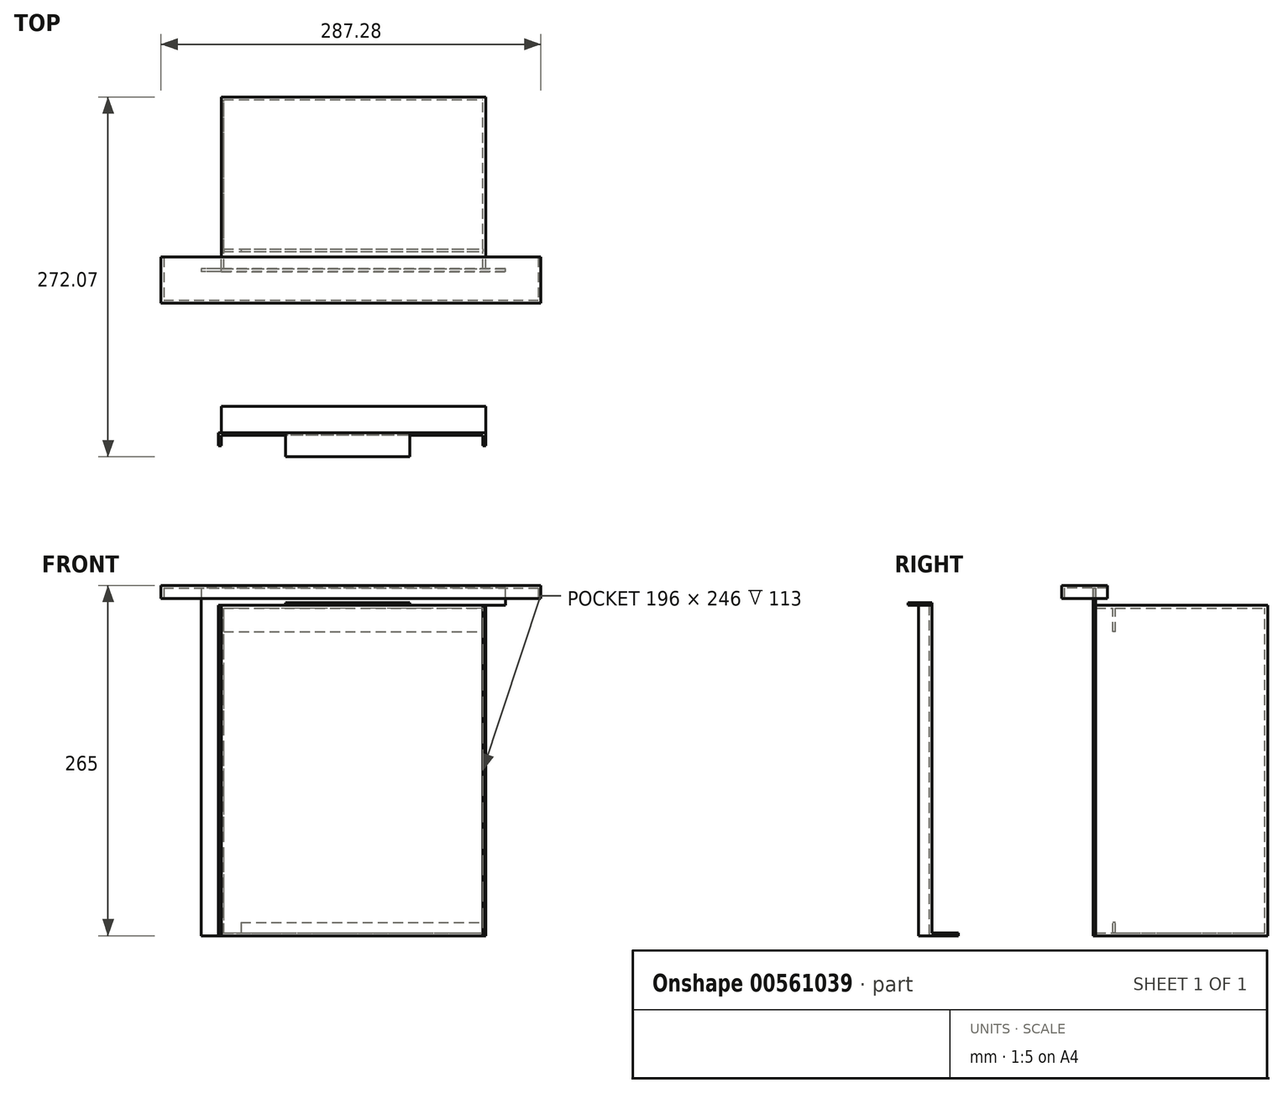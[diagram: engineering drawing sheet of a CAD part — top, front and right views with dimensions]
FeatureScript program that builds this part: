
annotation { "Feature Type Name" : "Feature", "Feature Type Description" : "" }
export const myFeature = defineFeature(function(context is Context, id is Id, definition is map)
    precondition{}
    {
        {
            var Q0;
            Q0=qCreatedBy(makeId("Front.planeOp"),FACE);
            var sketch = newSketch(context, id + "F0", { "sketchPlane" : qUnion([Q0])});
            skLineSegment(sketch, "E0.bottom", {"start": v(80.63, 0) * mm, "end": v(280.63, 0) * mm});
            skLineSegment(sketch, "E0.top", {"start": v(80.63, 250) * mm, "end": v(280.63, 250) * mm});
            skLineSegment(sketch, "E0.left", {"start": v(80.63, 0) * mm, "end": v(80.63, 250) * mm});
            skLineSegment(sketch, "E0.right", {"start": v(280.63, 0) * mm, "end": v(280.63, 250) * mm});
            skSolve(sketch);
        }
        {
            var Q0;
            Q0=makeQuery(id+"F0.imprint","IMPRINT",FACE,{"disambiguationData":[TD([[makeQuery(id+"F0.imprint","IMPRINT",EDGE,{"derivedFrom":sQuery(id+"F0.wireOp",EDGE,"E0.bottom")}),1.0]])]});
            extrude(context, id + "F1", {"entities" : qUnion([Q0]), "depth" : 130 * mm, "offsetDistance" : 25 * mm});
        }
        {
            var Q0;
            Q0=makeQuery(id+"F1.opExtrude","CAP_FACE",FACE,{"disambiguationData":[OSD([sQuery(id+"F0.wireOp",EDGE,"E0.bottom"),sQuery(id+"F0.wireOp",EDGE,"E0.top"),sQuery(id+"F0.wireOp",EDGE,"E0.left"),sQuery(id+"F0.wireOp",EDGE,"E0.right")])],"isStart":false});
            shell(context, id + "F2", {"entities" : qUnion([Q0]), "thickness" : 2 * mm});
        }
        {
            var Q0;
            Q0=makeQuery(id+"F2.opShell","OFFSET_FACE",FACE,{"disambiguationData":[OSD([sQuery(id+"F0.wireOp",EDGE,"E0.bottom"),sQuery(id+"F0.wireOp",EDGE,"E0.top"),sQuery(id+"F0.wireOp",EDGE,"E0.left"),sQuery(id+"F0.wireOp",EDGE,"E0.right")])]});
            cPlane(context, id + "F3", {"entities" : qUnion([Q0]), "cplaneType" : CPlaneType.OFFSET, "offset" : 115 * mm, "width" : 150 * mm, "height" : 150 * mm});
        }
        {
            var Q0;
            Q0=qCreatedBy(id+"F3.planeOp",FACE);
            var sketch = newSketch(context, id + "F4", { "sketchPlane" : qUnion([Q0])});
            skLineSegment(sketch, "E1.bottom", {"start": v(80.63, 250) * mm, "end": v(280.63, 250) * mm});
            skLineSegment(sketch, "E1.top", {"start": v(80.63, 230) * mm, "end": v(280.63, 230) * mm});
            skLineSegment(sketch, "E1.left", {"start": v(80.63, 250) * mm, "end": v(80.63, 230) * mm});
            skLineSegment(sketch, "E1.right", {"start": v(280.63, 250) * mm, "end": v(280.63, 230) * mm});
            skLineSegment(sketch, "E2.bottom", {"start": v(80.63, 230) * mm, "end": v(95.63, 230) * mm});
            skLineSegment(sketch, "E2.top", {"start": v(80.63, 0) * mm, "end": v(95.63, 0) * mm});
            skLineSegment(sketch, "E2.left", {"start": v(80.63, 230) * mm, "end": v(80.63, 0) * mm});
            skLineSegment(sketch, "E2.right", {"start": v(95.63, 230) * mm, "end": v(95.63, 0) * mm});
            skLineSegment(sketch, "E3.bottom", {"start": v(95.63, 0) * mm, "end": v(280.63, 0) * mm});
            skLineSegment(sketch, "E3.top", {"start": v(95.63, 10) * mm, "end": v(280.63, 10) * mm});
            skLineSegment(sketch, "E3.left", {"start": v(95.63, 0) * mm, "end": v(95.63, 10) * mm});
            skLineSegment(sketch, "E3.right", {"start": v(280.63, 0) * mm, "end": v(280.63, 10) * mm});
            skLineSegment(sketch, "E4.bottom", {"start": v(280.63, 10) * mm, "end": v(265.63, 10) * mm});
            skLineSegment(sketch, "E4.top", {"start": v(280.63, 230) * mm, "end": v(265.63, 230) * mm});
            skLineSegment(sketch, "E4.left", {"start": v(280.63, 10) * mm, "end": v(280.63, 230) * mm});
            skLineSegment(sketch, "E4.right", {"start": v(265.63, 10) * mm, "end": v(265.63, 230) * mm});
            skSolve(sketch);
        }
        {
            var Q0;
            Q0=makeQuery(id+"F4.imprint","IMPRINT",FACE,{"disambiguationData":[TD([[makeQuery(id+"F4.imprint","IMPRINT",EDGE,{"derivedFrom":sQuery(id+"F4.wireOp",EDGE,"E1.bottom")}),-1.0]])]});
            var Q1;
            Q1=makeQuery(id+"F4.imprint","IMPRINT",FACE,{"disambiguationData":[TD([[makeQuery(id+"F4.imprint","IMPRINT",EDGE,{"derivedFrom":sQuery(id+"F4.wireOp",EDGE,"E2.bottom")}),-1.0]])]});
            var Q2;
            Q2=makeQuery(id+"F4.imprint","IMPRINT",FACE,{"disambiguationData":[TD([[makeQuery(id+"F4.imprint","IMPRINT",EDGE,{"derivedFrom":sQuery(id+"F4.wireOp",EDGE,"E4.bottom")}),-1.0]])]});
            var Q3;
            Q3=makeQuery(id+"F4.imprint","IMPRINT",FACE,{"disambiguationData":[TD([[makeQuery(id+"F4.imprint","IMPRINT",EDGE,{"derivedFrom":sQuery(id+"F4.wireOp",EDGE,"E3.bottom")}),1.0]])]});
            extrude(context, id + "F5", {"entities" : qUnion([Q0, Q1, Q2, Q3]), "operationType" : NewBodyOperationType.ADD, "oppositeDirection" : true, "depth" : 2 * mm, "offsetDistance" : 25 * mm});
        }
        {
            var Q0;
            Q0=makeQuery(id+"F0.imprint","IMPRINT",FACE,{"disambiguationData":[TD([[makeQuery(id+"F0.imprint","IMPRINT",EDGE,{"derivedFrom":sQuery(id+"F0.wireOp",EDGE,"E0.bottom")}),1.0]])]});
            cPlane(context, id + "F6", {"entities" : qUnion([Q0]), "cplaneType" : CPlaneType.OFFSET, "offset" : 130 * mm, "width" : 150 * mm, "height" : 150 * mm});
        }
        {
            var Q0;
            Q0=qCreatedBy(id+"F6.planeOp",FACE);
            var sketch = newSketch(context, id + "F7", { "sketchPlane" : qUnion([Q0])});
            skLineSegment(sketch, "E5.bottom", {"start": v(80.63, 250) * mm, "end": v(65.63, 250) * mm});
            skLineSegment(sketch, "E5.top", {"start": v(80.63, 0) * mm, "end": v(65.63, 0) * mm});
            skLineSegment(sketch, "E5.left", {"start": v(80.63, 250) * mm, "end": v(80.63, 0) * mm});
            skLineSegment(sketch, "E5.right", {"start": v(65.63, 250) * mm, "end": v(65.63, 0) * mm});
            skLineSegment(sketch, "E6.bottom", {"start": v(65.63, 250) * mm, "end": v(295.63, 250) * mm});
            skLineSegment(sketch, "E6.top", {"start": v(65.63, 265) * mm, "end": v(295.63, 265) * mm});
            skLineSegment(sketch, "E6.left", {"start": v(65.63, 250) * mm, "end": v(65.63, 265) * mm});
            skLineSegment(sketch, "E6.right", {"start": v(295.63, 250) * mm, "end": v(295.63, 265) * mm});
            skLineSegment(sketch, "E7.bottom", {"start": v(295.63, 250) * mm, "end": v(280.63, 250) * mm});
            skLineSegment(sketch, "E7.top", {"start": v(295.63, 0) * mm, "end": v(280.63, 0) * mm});
            skLineSegment(sketch, "E7.left", {"start": v(295.63, 250) * mm, "end": v(295.63, 0) * mm});
            skLineSegment(sketch, "E7.right", {"start": v(280.63, 250) * mm, "end": v(280.63, 0) * mm});
            skLineSegment(sketch, "E8.top", {"start": v(280.63, 0) * mm, "end": v(65.63, 0) * mm});
            skLineSegment(sketch, "E8.left", {"start": v(280.63, 0) * mm, "end": v(280.63, 0) * mm});
            skSolve(sketch);
        }
        {
            var Q0;
            {var subQ0=sQuery(id+"F7.wireOp",EDGE,"E5.left");Q0=makeQuery(id+"F7.imprint","IMPRINT",FACE,{"disambiguationData":[TD([[makeQuery(id+"F7.imprint","IMPRINT",EDGE,{"derivedFrom":subQ0}),-1.0]])]});}
            var Q1;
            Q1=makeQuery(id+"F7.imprint","IMPRINT",FACE,{"disambiguationData":[TD([[makeQuery(id+"F7.imprint","IMPRINT",EDGE,{"derivedFrom":sQuery(id+"F7.wireOp",EDGE,"E6.top")}),-1.0]])]});
            var Q2;
            Q2=makeQuery(id+"F7.imprint","IMPRINT",FACE,{"disambiguationData":[TD([[makeQuery(id+"F7.imprint","IMPRINT",EDGE,{"derivedFrom":sQuery(id+"F7.wireOp",EDGE,"E7.bottom")}),1.0]])]});
            extrude(context, id + "F8", {"entities" : qUnion([Q0, Q1, Q2]), "operationType" : NewBodyOperationType.ADD, "depth" : 2 * mm, "offsetDistance" : 25 * mm});
        }
        {
            var Q0;
            Q0=makeQuery(id+"F0.imprint","IMPRINT",FACE,{"disambiguationData":[TD([[makeQuery(id+"F0.imprint","IMPRINT",EDGE,{"derivedFrom":sQuery(id+"F0.wireOp",EDGE,"E0.bottom")}),1.0]])]});
            cPlane(context, id + "F9", {"entities" : qUnion([Q0]), "cplaneType" : CPlaneType.OFFSET, "offset" : 254 * mm, "width" : 150 * mm, "height" : 150 * mm});
        }
        {
            var Q0;
            Q0=qCreatedBy(id+"F9.planeOp",FACE);
            var sketch = newSketch(context, id + "F10", { "sketchPlane" : qUnion([Q0])});
            skLineSegment(sketch, "E9.bottom", {"start": v(280.63, 250) * mm, "end": v(80.63, 250) * mm});
            skLineSegment(sketch, "E9.top", {"start": v(280.63, 0) * mm, "end": v(80.63, 0) * mm});
            skLineSegment(sketch, "E9.left", {"start": v(280.63, 250) * mm, "end": v(280.63, 0) * mm});
            skLineSegment(sketch, "E9.right", {"start": v(80.63, 250) * mm, "end": v(80.63, 0) * mm});
            skSolve(sketch);
        }
        {
            var Q0;
            Q0=makeQuery(id+"F10.imprint","IMPRINT",FACE,{"disambiguationData":[TD([[makeQuery(id+"F10.imprint","IMPRINT",EDGE,{"derivedFrom":sQuery(id+"F10.wireOp",EDGE,"E9.bottom")}),1.0]])]});
            extrude(context, id + "F11", {"entities" : qUnion([Q0]), "depth" : 2 * mm, "offsetDistance" : 25 * mm});
        }
        {
            var Q0;
            Q0=sQuery(id+"F10.wireOp",EDGE,"E9.right");
            cPlane(context, id + "F12", {"entities" : qUnion([Q0]), "cplaneType" : CPlaneType.LINE_ANGLE, "offset" : 25 * mm, "angle" : 0 * degree, "width" : 150 * mm, "height" : 150 * mm});
        }
        {
            var Q0;
            Q0=sQuery(id+"F10.wireOp",EDGE,"E9.left");
            cPlane(context, id + "F13", {"entities" : qUnion([Q0]), "cplaneType" : CPlaneType.LINE_ANGLE, "offset" : 25 * mm, "angle" : 0 * degree, "width" : 150 * mm, "height" : 150 * mm});
        }
        {
            var Q0;
            Q0=sQuery(id+"F10.wireOp",EDGE,"E9.top");
            cPlane(context, id + "F14", {"entities" : qUnion([Q0]), "cplaneType" : CPlaneType.LINE_ANGLE, "offset" : 25 * mm, "angle" : 90 * degree, "width" : 150 * mm, "height" : 150 * mm});
        }
        {
            var Q0;
            Q0=qCreatedBy(id+"F12.planeOp",FACE);
            var sketch = newSketch(context, id + "F15", { "sketchPlane" : qUnion([Q0])});
            skLineSegment(sketch, "E10.bottom", {"start": v(254, 250) * mm, "end": v(264, 250) * mm});
            skLineSegment(sketch, "E10.top", {"start": v(254, 0) * mm, "end": v(264, 0) * mm});
            skLineSegment(sketch, "E10.left", {"start": v(254, 250) * mm, "end": v(254, 0) * mm});
            skLineSegment(sketch, "E10.right", {"start": v(264, 250) * mm, "end": v(264, 0) * mm});
            skSolve(sketch);
        }
        {
            var Q0;
            Q0=makeQuery(id+"F15.imprint","IMPRINT",FACE,{"disambiguationData":[TD([[makeQuery(id+"F15.imprint","IMPRINT",EDGE,{"derivedFrom":sQuery(id+"F15.wireOp",EDGE,"E10.bottom")}),-1.0]])]});
            extrude(context, id + "F16", {"entities" : qUnion([Q0]), "operationType" : NewBodyOperationType.ADD, "depth" : 2 * mm, "offsetDistance" : 25 * mm});
        }
        {
            var Q0;
            Q0=qCreatedBy(id+"F13.planeOp",FACE);
            var sketch = newSketch(context, id + "F17", { "sketchPlane" : qUnion([Q0])});
            skLineSegment(sketch, "E11.bottom", {"start": v(254, 250) * mm, "end": v(264, 250) * mm});
            skLineSegment(sketch, "E11.top", {"start": v(254, 0) * mm, "end": v(264, 0) * mm});
            skLineSegment(sketch, "E11.left", {"start": v(254, 250) * mm, "end": v(254, 0) * mm});
            skLineSegment(sketch, "E11.right", {"start": v(264, 250) * mm, "end": v(264, 0) * mm});
            skSolve(sketch);
        }
        {
            var Q0;
            Q0=makeQuery(id+"F17.imprint","IMPRINT",FACE,{"disambiguationData":[TD([[makeQuery(id+"F17.imprint","IMPRINT",EDGE,{"derivedFrom":sQuery(id+"F17.wireOp",EDGE,"E11.bottom")}),-1.0]])]});
            extrude(context, id + "F18", {"entities" : qUnion([Q0]), "operationType" : NewBodyOperationType.ADD, "depth" : 2 * mm, "offsetDistance" : 25 * mm});
        }
        {
            var Q0;
            Q0=qCreatedBy(id+"F14.planeOp",FACE);
            var sketch = newSketch(context, id + "F19", { "sketchPlane" : qUnion([Q0])});
            skLineSegment(sketch, "E12.bottom", {"start": v(80.63, -234) * mm, "end": v(280.63, -234) * mm});
            skLineSegment(sketch, "E12.top", {"start": v(80.63, -254) * mm, "end": v(280.63, -254) * mm});
            skLineSegment(sketch, "E12.left", {"start": v(80.63, -234) * mm, "end": v(80.63, -254) * mm});
            skLineSegment(sketch, "E12.right", {"start": v(280.63, -234) * mm, "end": v(280.63, -254) * mm});
            skSolve(sketch);
        }
        {
            var Q0;
            Q0=makeQuery(id+"F19.imprint","IMPRINT",FACE,{"disambiguationData":[TD([[makeQuery(id+"F19.imprint","IMPRINT",EDGE,{"derivedFrom":sQuery(id+"F19.wireOp",EDGE,"E12.bottom")}),-1.0]])]});
            extrude(context, id + "F20", {"entities" : qUnion([Q0]), "operationType" : NewBodyOperationType.ADD, "depth" : 2 * mm, "offsetDistance" : 25 * mm});
        }
        {
            var Q0;
            Q0=makeQuery(id+"F7.imprint","IMPRINT",FACE,{"disambiguationData":[TD([[makeQuery(id+"F7.imprint","IMPRINT",EDGE,{"derivedFrom":sQuery(id+"F7.wireOp",EDGE,"E6.top")}),-1.0]])]});
            cPlane(context, id + "F21", {"entities" : qUnion([Q0]), "cplaneType" : CPlaneType.OFFSET, "offset" : 8.9 * mm, "oppositeDirection" : true, "width" : 150 * mm, "height" : 150 * mm});
        }
        {
            var Q0;
            Q0=qCreatedBy(id+"F21.planeOp",FACE);
            var sketch = newSketch(context, id + "F22", { "sketchPlane" : qUnion([Q0])});
            skLineSegment(sketch, "E13.bottom", {"start": v(37.17, 265) * mm, "end": v(320.45, 265) * mm});
            skLineSegment(sketch, "E13.top", {"start": v(37.17, 250) * mm, "end": v(320.45, 250) * mm});
            skLineSegment(sketch, "E13.left", {"start": v(37.17, 265) * mm, "end": v(37.17, 250) * mm});
            skLineSegment(sketch, "E13.right", {"start": v(320.45, 265) * mm, "end": v(320.45, 250) * mm});
            skSolve(sketch);
        }
        {
            var Q0;
            Q0=sQuery(id+"F22.wireOp",EDGE,"E13.bottom");
            cPlane(context, id + "F23", {"entities" : qUnion([Q0]), "cplaneType" : CPlaneType.LINE_ANGLE, "offset" : 25 * mm, "angle" : 90 * degree, "width" : 150 * mm, "height" : 150 * mm});
        }
        {
            var Q0;
            Q0=sQuery(id+"F10.wireOp",EDGE,"E9.bottom");
            cPlane(context, id + "F24", {"entities" : qUnion([Q0]), "cplaneType" : CPlaneType.LINE_ANGLE, "offset" : 25 * mm, "angle" : 90 * degree, "width" : 150 * mm, "height" : 150 * mm});
        }
        {
            var Q0;
            Q0=qCreatedBy(id+"F24.planeOp",FACE);
            var sketch = newSketch(context, id + "F25", { "sketchPlane" : qUnion([Q0])});
            skLineSegment(sketch, "E14.bottom", {"start": v(129.18, -272.07) * mm, "end": v(223.2, -272.07) * mm});
            skLineSegment(sketch, "E14.top", {"start": v(129.18, -254) * mm, "end": v(223.2, -254) * mm});
            skLineSegment(sketch, "E14.left", {"start": v(129.18, -272.07) * mm, "end": v(129.18, -254) * mm});
            skLineSegment(sketch, "E14.right", {"start": v(223.2, -272.07) * mm, "end": v(223.2, -254) * mm});
            skSolve(sketch);
        }
        {
            var Q0;
            Q0=makeQuery(id+"F25.imprint","IMPRINT",FACE,{"disambiguationData":[TD([[makeQuery(id+"F25.imprint","IMPRINT",EDGE,{"derivedFrom":sQuery(id+"F25.wireOp",EDGE,"E14.bottom")}),1.0]])]});
            extrude(context, id + "F26", {"entities" : qUnion([Q0]), "operationType" : NewBodyOperationType.ADD, "depth" : 2 * mm, "offsetDistance" : 25 * mm});
        }
        {
            var Q0;
            Q0=qCreatedBy(id+"F23.planeOp",FACE);
            var sketch = newSketch(context, id + "F27", { "sketchPlane" : qUnion([Q0])});
            skLineSegment(sketch, "E15.bottom", {"start": v(37.17, -121.1) * mm, "end": v(320.45, -121.1) * mm});
            skLineSegment(sketch, "E15.top", {"start": v(37.17, -153.75) * mm, "end": v(320.45, -153.75) * mm});
            skLineSegment(sketch, "E15.left", {"start": v(37.17, -121.1) * mm, "end": v(37.17, -153.75) * mm});
            skLineSegment(sketch, "E15.right", {"start": v(320.45, -121.1) * mm, "end": v(320.45, -153.75) * mm});
            skSolve(sketch);
        }
        {
            var Q0;
            Q0=makeQuery(id+"F27.imprint","IMPRINT",FACE,{"disambiguationData":[TD([[makeQuery(id+"F27.imprint","IMPRINT",EDGE,{"derivedFrom":sQuery(id+"F27.wireOp",EDGE,"E15.bottom")}),-1.0]])]});
            extrude(context, id + "F28", {"entities" : qUnion([Q0]), "operationType" : NewBodyOperationType.ADD, "oppositeDirection" : true, "depth" : 2 * mm, "offsetDistance" : 25 * mm});
        }
        {
            var Q0;
            Q0=sQuery(id+"F27.wireOp",EDGE,"E15.right");
            cPlane(context, id + "F29", {"entities" : qUnion([Q0]), "cplaneType" : CPlaneType.LINE_ANGLE, "offset" : 25 * mm, "angle" : 90 * degree, "width" : 150 * mm, "height" : 150 * mm});
        }
        {
            var Q0;
            Q0=qCreatedBy(id+"F29.planeOp",FACE);
            var sketch = newSketch(context, id + "F30", { "sketchPlane" : qUnion([Q0])});
            skLineSegment(sketch, "E16.bottom", {"start": v(-153.75, 265) * mm, "end": v(-121.1, 265) * mm});
            skLineSegment(sketch, "E16.top", {"start": v(-153.75, 255) * mm, "end": v(-121.1, 255) * mm});
            skLineSegment(sketch, "E16.left", {"start": v(-153.75, 265) * mm, "end": v(-153.75, 255) * mm});
            skLineSegment(sketch, "E16.right", {"start": v(-121.1, 265) * mm, "end": v(-121.1, 255) * mm});
            skSolve(sketch);
        }
        {
            var Q0;
            Q0=makeQuery(id+"F30.imprint","IMPRINT",FACE,{"disambiguationData":[TD([[makeQuery(id+"F30.imprint","IMPRINT",EDGE,{"derivedFrom":sQuery(id+"F30.wireOp",EDGE,"E16.bottom")}),-1.0]])]});
            extrude(context, id + "F31", {"entities" : qUnion([Q0]), "operationType" : NewBodyOperationType.ADD, "depth" : 2 * mm, "offsetDistance" : 25 * mm});
        }
        {
            var Q0;
            Q0=sQuery(id+"F27.wireOp",EDGE,"E15.left");
            cPlane(context, id + "F32", {"entities" : qUnion([Q0]), "cplaneType" : CPlaneType.LINE_ANGLE, "offset" : 25 * mm, "angle" : 90 * degree, "width" : 150 * mm, "height" : 150 * mm});
        }
        {
            var Q0;
            Q0=qCreatedBy(id+"F32.planeOp",FACE);
            var sketch = newSketch(context, id + "F33", { "sketchPlane" : qUnion([Q0])});
            skLineSegment(sketch, "E17.bottom", {"start": v(-153.75, 265) * mm, "end": v(-121.1, 265) * mm});
            skLineSegment(sketch, "E17.top", {"start": v(-153.75, 255) * mm, "end": v(-121.1, 255) * mm});
            skLineSegment(sketch, "E17.left", {"start": v(-153.75, 265) * mm, "end": v(-153.75, 255) * mm});
            skLineSegment(sketch, "E17.right", {"start": v(-121.1, 265) * mm, "end": v(-121.1, 255) * mm});
            skSolve(sketch);
        }
        {
            var Q0;
            Q0=makeQuery(id+"F33.imprint","IMPRINT",FACE,{"disambiguationData":[TD([[makeQuery(id+"F33.imprint","IMPRINT",EDGE,{"derivedFrom":sQuery(id+"F33.wireOp",EDGE,"E17.bottom")}),-1.0]])]});
            extrude(context, id + "F34", {"entities" : qUnion([Q0]), "operationType" : NewBodyOperationType.ADD, "oppositeDirection" : true, "depth" : 2 * mm, "offsetDistance" : 25 * mm});
        }
        {
            var Q0;
            Q0=sQuery(id+"F27.wireOp",EDGE,"E15.top");
            cPlane(context, id + "F35", {"entities" : qUnion([Q0]), "cplaneType" : CPlaneType.LINE_ANGLE, "offset" : 25 * mm, "angle" : 0 * degree, "width" : 150 * mm, "height" : 150 * mm});
        }
        {
            var Q0;
            Q0=qCreatedBy(id+"F35.planeOp",FACE);
            var sketch = newSketch(context, id + "F36", { "sketchPlane" : qUnion([Q0])});
            skLineSegment(sketch, "E18.bottom", {"start": v(-35.17, 255) * mm, "end": v(-322.45, 255) * mm});
            skLineSegment(sketch, "E18.top", {"start": v(-35.17, 265) * mm, "end": v(-322.45, 265) * mm});
            skLineSegment(sketch, "E18.left", {"start": v(-35.17, 255) * mm, "end": v(-35.17, 265) * mm});
            skLineSegment(sketch, "E18.right", {"start": v(-322.45, 255) * mm, "end": v(-322.45, 265) * mm});
            skSolve(sketch);
        }
        {
            var Q0;
            Q0=makeQuery(id+"F36.imprint","IMPRINT",FACE,{"disambiguationData":[TD([[makeQuery(id+"F36.imprint","IMPRINT",EDGE,{"derivedFrom":sQuery(id+"F36.wireOp",EDGE,"E18.bottom")}),-1.0]])]});
            extrude(context, id + "F37", {"entities" : qUnion([Q0]), "operationType" : NewBodyOperationType.ADD, "oppositeDirection" : true, "depth" : 2 * mm, "offsetDistance" : 25 * mm});
        }
        {
            var Q0;
            Q0=makeQuery(id+"F0.imprint","IMPRINT",FACE,{"disambiguationData":[TD([[makeQuery(id+"F0.imprint","IMPRINT",EDGE,{"derivedFrom":sQuery(id+"F0.wireOp",EDGE,"E0.bottom")}),1.0]])]});
            cPlane(context, id + "F38", {"entities" : qUnion([Q0]), "cplaneType" : CPlaneType.OFFSET, "offset" : 650 * mm, "width" : 150 * mm, "height" : 150 * mm});
        }
    });
